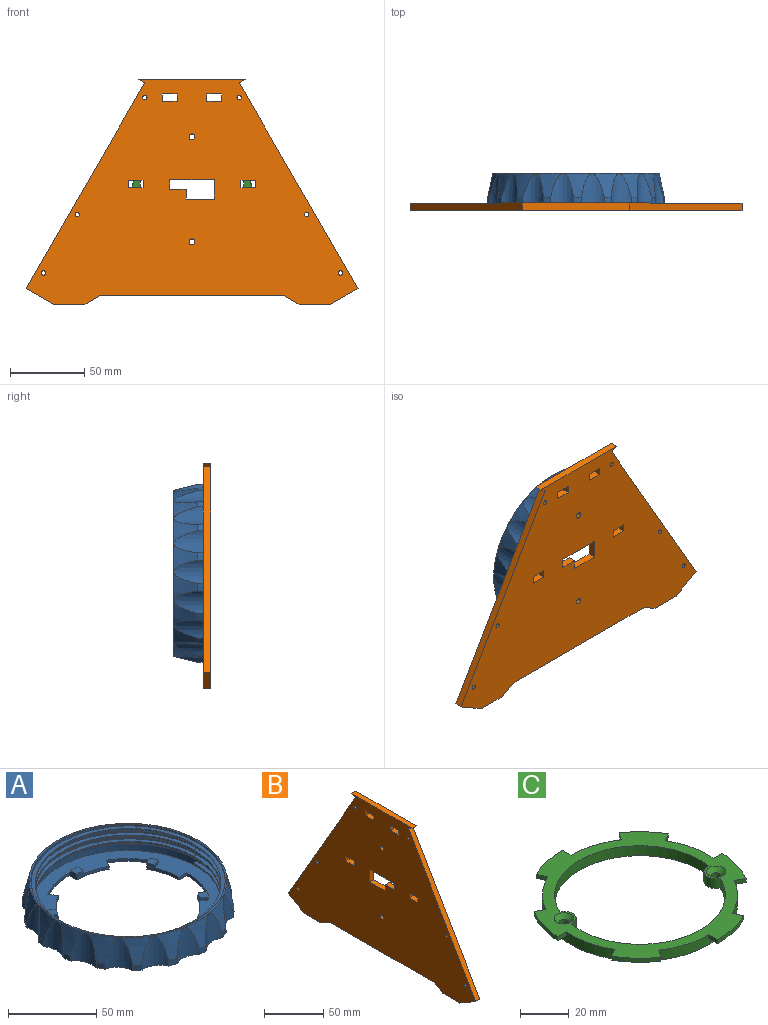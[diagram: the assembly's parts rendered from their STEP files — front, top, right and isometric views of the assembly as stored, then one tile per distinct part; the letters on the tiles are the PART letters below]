
ASSEMBLY  parts=3 mates=1
PART A: 105 faces, bbox 122.7x126.8x23 mm
  f0: plane 5.6x5.31mm, normal (0,0,1), area 26.5mm2, adj f1,f2,f3,f4
  f1: plane 4.96x2mm, normal (0.99,-0.12,0), area 10mm2, adj f0,f2,f4,f5
  f2: cylinder r=46mm len=5.6mm, axis (0,0,-1), area 11.2mm2, adj f0,f1,f3,f5
  f3: plane 6.25x4mm, normal (-1,0,0), area 22.5mm2, adj f0,f2,f4,f5,f37,f38,f48
  f4: cylinder r=41mm len=4.99mm, axis (0,0,-1), area 10mm2, adj f0,f1,f3,f5
  f5: plane 110x110mm, normal (0,0,1), area 3265.8mm2, adj f1,f2,f3,f4,f8,f10,f11,f12
  f6: cylinder r=55mm len=110mm, axis (0,0,-1), area 345.6mm2, adj f7,f9,f96,f98
  f7: cylinder r=55mm len=110mm, axis (0,0,-1), area 345.6mm2, adj f6,f8,f92,f94
  f8: cylinder r=55mm len=110mm, axis (0,0,-1), area 950.3mm2, adj f5,f7,f49,f50
  f9: cylinder r=55mm len=110mm, axis (0,0,-1), area 614.4mm2, adj f6,f99,f100,f102,f103
  f10: plane 5.41x4mm, normal (0.5,0.87,0), area 22.5mm2, adj f5,f11,f13,f14,f47,f48,f51
  f11: cylinder r=46mm len=4.68mm, axis (0,0,-1), area 11.2mm2, adj f5,f10,f12,f51
  f12: plane 3.99x3.01mm, normal (-0.6,-0.8,0), area 10mm2, adj f5,f11,f13,f51
  f13: cylinder r=41mm len=4.17mm, axis (0,0,-1), area 10mm2, adj f5,f10,f12,f51
  f14: cylinder r=40.75mm len=14.92mm, axis (0,0,-1), area 42.7mm2, adj f5,f10,f15,f48
  f15: plane 5.41x3.13mm, normal (-0.87,-0.5,0), area 12.5mm2, adj f5,f14,f16,f48
  f16: cylinder r=47mm len=23.5mm, axis (0,0,1), area 49.2mm2, adj f5,f15,f17,f48
  f17: plane 6.25x4mm, normal (1,0,0), area 22.5mm2, adj f5,f16,f18,f20,f21,f48,f52
  f18: cylinder r=46mm len=5.6mm, axis (0,0,-1), area 11.2mm2, adj f5,f17,f19,f52
  f19: plane 4.96x2mm, normal (-0.99,0.12,0), area 10mm2, adj f5,f18,f20,f52
  f20: cylinder r=41mm len=4.99mm, axis (0,0,-1), area 10mm2, adj f5,f17,f19,f52
  f21: cylinder r=40.75mm len=20.38mm, axis (0,0,-1), area 42.7mm2, adj f5,f17,f22,f48
  f22: plane 5.41x3.13mm, normal (-0.87,0.5,0), area 12.5mm2, adj f5,f21,f23,f48
  f23: cylinder r=47mm len=17.2mm, axis (0,0,1), area 49.2mm2, adj f5,f22,f24,f48
  f24: plane 5.41x4mm, normal (0.5,-0.87,0), area 22.5mm2, adj f5,f23,f25,f27,f28,f48,f53
  f25: cylinder r=46mm len=5.02mm, axis (0,0,-1), area 11.2mm2, adj f5,f24,f26,f53
  f26: plane 4.6x2mm, normal (-0.39,0.92,0), area 10mm2, adj f5,f25,f27,f53
  f27: cylinder r=41mm len=4.47mm, axis (0,0,-1), area 10mm2, adj f5,f24,f26,f53
  f28: cylinder r=40.75mm len=20.38mm, axis (0,0,-1), area 42.7mm2, adj f5,f24,f29,f48
  f29: plane 6.25x2mm, normal (0,1,0), area 12.5mm2, adj f5,f28,f30,f48
  f30: cylinder r=47mm len=23.5mm, axis (0,0,1), area 49.2mm2, adj f5,f29,f31,f48
  f31: plane 5.41x4mm, normal (-0.5,-0.87,0), area 22.5mm2, adj f5,f30,f32,f34,f35,f48,f54
  f32: cylinder r=46mm len=4.68mm, axis (0,0,-1), area 11.2mm2, adj f5,f31,f33,f54
  f33: plane 3.99x3.01mm, normal (0.6,0.8,0), area 10mm2, adj f5,f32,f34,f54
  f34: cylinder r=41mm len=4.17mm, axis (0,0,-1), area 10mm2, adj f5,f31,f33,f54
  f35: cylinder r=40.75mm len=14.92mm, axis (0,0,-1), area 42.7mm2, adj f5,f31,f36,f48
  f36: plane 5.41x3.13mm, normal (0.87,0.5,0), area 12.5mm2, adj f5,f35,f37,f48
  f37: cylinder r=47mm len=23.5mm, axis (0,0,1), area 49.2mm2, adj f3,f5,f36,f48
  f38: cylinder r=40.75mm len=20.38mm, axis (0,0,-1), area 42.7mm2, adj f3,f5,f39,f48
  f39: plane 5.41x3.13mm, normal (0.87,-0.5,0), area 12.5mm2, adj f5,f38,f40,f48
  f40: cylinder r=47mm len=17.2mm, axis (0,0,1), area 49.2mm2, adj f5,f39,f41,f48
  f41: plane 5.41x4mm, normal (-0.5,0.87,0), area 22.5mm2, adj f5,f40,f42,f44,f45,f48,f55
  f42: cylinder r=46mm len=5.02mm, axis (0,0,-1), area 11.2mm2, adj f5,f41,f43,f55
  f43: plane 4.6x2mm, normal (0.39,-0.92,0), area 10mm2, adj f5,f42,f44,f55
  f44: cylinder r=41mm len=4.47mm, axis (0,0,-1), area 10mm2, adj f5,f41,f43,f55
  f45: cylinder r=40.75mm len=20.38mm, axis (0,0,-1), area 42.7mm2, adj f5,f41,f46,f48
  f46: plane 6.25x2mm, normal (0,-1,0), area 12.5mm2, adj f5,f45,f47,f48
  f47: cylinder r=47mm len=23.5mm, axis (0,0,1), area 49.2mm2, adj f5,f10,f46,f48
  f48: plane 120x119mm, normal (0,0,-1), area 4655.6mm2, adj f3,f10,f14,f15,f16,f17,f21,f22
  f49: bspline ~126.76x117.75mm, area 1194.1mm2, adj f8,f50,f92,f93
  f50: plane 3.5x2.5mm, normal (0,1,0), area 5.6mm2, adj f8,f49,f93,f94
  f51: plane 7.18x7.09mm, normal (0,0,1), area 26.5mm2, adj f10,f11,f12,f13
  f52: plane 5.6x5.31mm, normal (0,0,1), area 26.5mm2, adj f17,f18,f19,f20
  f53: plane 6.97x6.83mm, normal (0,0,1), area 26.5mm2, adj f24,f25,f26,f27
  f54: plane 7.18x7.09mm, normal (0,0,1), area 26.5mm2, adj f31,f32,f33,f34
  f55: plane 6.97x6.83mm, normal (0,0,1), area 26.5mm2, adj f41,f42,f43,f44
  f56: cylinder r=60mm len=5.34mm, axis (0,0,1), area 19.1mm2, adj f48,f57,f91,f95
  f57: cone r=13mm half-angle=2.6deg, axis (0,0,1), area 245.3mm2, adj f48,f56,f58,f95
  f58: cylinder r=60mm len=4.69mm, axis (0,0,1), area 19.1mm2, adj f48,f57,f59,f95
  f59: cone r=13mm half-angle=2.6deg, axis (0,0,1), area 245.3mm2, adj f48,f58,f60,f95
  f60: cylinder r=60mm len=4.15mm, axis (0,0,1), area 19.1mm2, adj f48,f59,f61,f95
  f61: cone r=13mm half-angle=2.6deg, axis (0,0,1), area 245.3mm2, adj f48,f60,f62,f95
  f62: cylinder r=60mm len=5.09mm, axis (0,0,1), area 19.1mm2, adj f48,f61,f63,f95
  f63: cone r=13mm half-angle=2.6deg, axis (0,0,1), area 245.3mm2, adj f48,f62,f64,f95
  f64: cylinder r=60mm len=5.42mm, axis (0,0,1), area 19.1mm2, adj f48,f63,f65,f95
  f65: cone r=13mm half-angle=2.6deg, axis (0,0,1), area 245.3mm2, adj f48,f64,f66,f95
  f66: cylinder r=60mm len=5.09mm, axis (0,0,1), area 19.1mm2, adj f48,f65,f67,f95
  f67: cone r=13mm half-angle=2.6deg, axis (0,0,1), area 245.3mm2, adj f48,f66,f68,f95
  f68: cylinder r=60mm len=4.15mm, axis (0,0,1), area 19.1mm2, adj f48,f67,f69,f95
  f69: cone r=13mm half-angle=2.6deg, axis (0,0,1), area 245.3mm2, adj f48,f68,f70,f95
  f70: cylinder r=60mm len=4.69mm, axis (0,0,1), area 19.1mm2, adj f48,f69,f71,f95
  f71: cone r=13mm half-angle=2.6deg, axis (0,0,1), area 245.3mm2, adj f48,f70,f72,f95
  f72: cylinder r=60mm len=5.34mm, axis (0,0,1), area 19.1mm2, adj f48,f71,f73,f95
  f73: cone r=13mm half-angle=2.6deg, axis (0,0,1), area 245.3mm2, adj f48,f72,f74,f95
  f74: cylinder r=60mm len=5.34mm, axis (0,0,1), area 19.1mm2, adj f48,f73,f75,f95
  f75: cone r=13mm half-angle=2.6deg, axis (0,0,1), area 245.3mm2, adj f48,f74,f76,f95
  f76: cylinder r=60mm len=4.69mm, axis (0,0,1), area 19.1mm2, adj f48,f75,f77,f95
  f77: cone r=13mm half-angle=2.6deg, axis (0,0,1), area 245.3mm2, adj f48,f76,f78,f95
  f78: cylinder r=60mm len=4.15mm, axis (0,0,1), area 19.1mm2, adj f48,f77,f79,f95
  f79: cone r=13mm half-angle=2.6deg, axis (0,0,1), area 245.3mm2, adj f48,f78,f80,f95
  f80: cylinder r=60mm len=5.09mm, axis (0,0,1), area 19.1mm2, adj f48,f79,f81,f95
  f81: cone r=13mm half-angle=2.6deg, axis (0,0,1), area 245.3mm2, adj f48,f80,f82,f95
  f82: cylinder r=60mm len=5.42mm, axis (0,0,1), area 19.1mm2, adj f48,f81,f83,f95
  f83: cone r=13mm half-angle=2.6deg, axis (0,0,1), area 245.3mm2, adj f48,f82,f84,f95
  f84: cylinder r=60mm len=5.09mm, axis (0,0,1), area 19.1mm2, adj f48,f83,f85,f95
  f85: cone r=13mm half-angle=2.6deg, axis (0,0,1), area 245.3mm2, adj f48,f84,f86,f95
  f86: cylinder r=60mm len=4.15mm, axis (0,0,1), area 19.1mm2, adj f48,f85,f87,f95
  f87: cone r=13mm half-angle=2.6deg, axis (0,0,1), area 245.3mm2, adj f48,f86,f88,f95
  f88: cylinder r=60mm len=4.69mm, axis (0,0,1), area 19.1mm2, adj f48,f87,f89,f95
  f89: cone r=13mm half-angle=2.6deg, axis (0,0,1), area 245.3mm2, adj f48,f88,f90,f95
  f90: cylinder r=60mm len=5.34mm, axis (0,0,1), area 19.1mm2, adj f48,f89,f91,f95
  f91: cone r=13mm half-angle=2.6deg, axis (0,0,1), area 245.3mm2, adj f48,f56,f90,f95
  f92: bspline ~126.76x117.75mm, area 1194.1mm2, adj f7,f49,f96,f97
  f93: bspline ~120.78x112.2mm, area 329.9mm2, adj f49,f50,f94,f97
  f94: bspline ~126.76x117.75mm, area 844.4mm2, adj f7,f50,f93,f98
  f95: cone r=60mm half-angle=13.8deg, axis (0,0,-1), area 2860.6mm2, adj f56,f57,f58,f59,f60,f61,f62,f63
  f96: bspline ~126.76x117.75mm, area 1194.1mm2, adj f6,f92,f100,f101
  f97: bspline ~120.78x112.2mm, area 329.9mm2, adj f92,f93,f98,f101
  f98: bspline ~126.76x117.75mm, area 844.4mm2, adj f6,f94,f97,f102
  f99: plane 112x112mm, normal (0,0,1), area 348.7mm2, adj f9,f95
  f100: bspline ~126.76x117.75mm, area 466.9mm2, adj f9,f96,f103,f104
  f101: bspline ~120.78x112.2mm, area 320.7mm2, adj f96,f97,f102,f103,f104
  f102: bspline ~126.76x117.75mm, area 750.6mm2, adj f9,f98,f101,f103
  f103: plane 110x102.64mm, normal (0,0,1), area 424mm2, adj f9,f100,f101,f102,f104
  f104: bspline ~112.2x97.04mm, area 9.2mm2, adj f100,f101,f103
PART B: 44 faces, bbox 5x223.7x152.1 mm
  f0: plane 5x5mm, normal (0,-1,0), area 25mm2, adj f1,f33,f34,f35
  f1: plane 10x5mm, normal (0,0,1), area 50mm2, adj f0,f2,f34,f35
  f2: plane 5x5mm, normal (0,1,0), area 25mm2, adj f1,f33,f34,f35
  f3: plane 124.79x5mm, normal (0,0,-1), area 623.9mm2, adj f4,f22,f34,f35
  f4: plane 10.39x6mm, normal (0,-0.5,-0.87), area 60mm2, adj f3,f5,f34,f35
  f5: plane 20x5mm, normal (0,0,-1), area 100mm2, adj f4,f6,f34,f35
  f6: plane 19.05x11mm, normal (0,0.5,-0.87), area 110mm2, adj f5,f7,f34,f35
  f7: plane 138.56x80.03mm, normal (0,0.87,0.5), area 800mm2, adj f6,f8,f34,f35
  f8: plane 5x4.33mm, normal (0,0.5,-0.87), area 25mm2, adj f7,f9,f34,f35
  f9: plane 72.27x5mm, normal (0,0,1), area 361.3mm2, adj f8,f10,f34,f35
  f10: plane 5x4.33mm, normal (0,-0.5,-0.87), area 25mm2, adj f9,f11,f34,f35
  f11: plane 138.56x80.03mm, normal (0,-0.87,0.5), area 800mm2, adj f10,f12,f34,f35
  f12: plane 19.05x11mm, normal (0,-0.5,-0.87), area 110mm2, adj f11,f13,f34,f35
  f13: plane 20x5mm, normal (0,0,-1), area 100mm2, adj f12,f22,f34,f35
  f14: plane 10x5mm, normal (0,0,1), area 50mm2, adj f15,f23,f34,f35
  f15: plane 5x5mm, normal (0,1,0), area 25mm2, adj f14,f16,f34,f35
  f16: plane 10x5mm, normal (0,0,-1), area 50mm2, adj f15,f23,f34,f35
  f17: plane 11x5mm, normal (0,0,1), area 55mm2, adj f18,f32,f34,f35
  f18: plane 6.5x5mm, normal (0,1,0), area 32.5mm2, adj f17,f19,f34,f35
  f19: plane 30x5mm, normal (0,0,-1), area 150mm2, adj f18,f20,f34,f35
  f20: plane 13x5mm, normal (0,-1,0), area 65mm2, adj f19,f21,f34,f35
  f21: plane 19x5mm, normal (0,0,1), area 95mm2, adj f20,f32,f34,f35
  f22: plane 10.39x6mm, normal (0,0.5,-0.87), area 60mm2, adj f3,f13,f34,f35
  f23: plane 5x5mm, normal (0,-1,0), area 25mm2, adj f14,f16,f34,f35
  f24: cylinder r=1.5mm len=5mm, axis (-1,0,0), area 47.1mm2, adj f34,f35
  f25: cylinder r=1.5mm len=5mm, axis (-1,0,0), area 47.1mm2, adj f34,f35
  f26: cylinder r=1.5mm len=5mm, axis (-1,0,0), area 47.1mm2, adj f34,f35
  f27: cylinder r=1.5mm len=5mm, axis (-1,0,0), area 47.1mm2, adj f34,f35
  f28: cylinder r=1.5mm len=5mm, axis (-1,0,0), area 47.1mm2, adj f34,f35
  f29: cylinder r=1.5mm len=5mm, axis (-1,0,0), area 47.1mm2, adj f34,f35
  f30: cylinder r=2mm len=5mm, axis (-1,0,0), area 62.8mm2, adj f34,f35
  f31: cylinder r=2mm len=5mm, axis (-1,0,0), area 62.8mm2, adj f34,f35
  f32: plane 6.5x5mm, normal (0,1,0), area 32.5mm2, adj f17,f21,f34,f35
  f33: plane 10x5mm, normal (0,0,-1), area 50mm2, adj f0,f2,f34,f35
  f34: plane 223.66x152.06mm, normal (1,0,0), area 20925.7mm2, adj f0,f1,f2,f3,f4,f5,f6,f7
  f35: plane 223.66x152.06mm, normal (-1,0,0), area 20925.7mm2, adj f0,f1,f2,f3,f4,f5,f6,f7
  f36: plane 5x5mm, normal (0,1,0), area 25mm2, adj f34,f35,f37,f39
  f37: plane 10x5mm, normal (0,0,1), area 50mm2, adj f34,f35,f36,f38
  f38: plane 5x5mm, normal (0,-1,0), area 25mm2, adj f34,f35,f37,f39
  f39: plane 10x5mm, normal (0,0,-1), area 50mm2, adj f34,f35,f36,f38
  f40: plane 5x5mm, normal (0,1,0), area 25mm2, adj f34,f35,f41,f43
  f41: plane 10x5mm, normal (0,0,1), area 50mm2, adj f34,f35,f40,f42
  f42: plane 5x5mm, normal (0,-1,0), area 25mm2, adj f34,f35,f41,f43
  f43: plane 10x5mm, normal (0,0,-1), area 50mm2, adj f34,f35,f40,f42
PART C: 35 faces, bbox 89.8x90x5 mm
  f0: cylinder r=2mm len=4mm, axis (0,0,-1), area 37.7mm2, adj f1,f2
  f1: cone r=2mm half-angle=45deg, axis (0,0,1), area 53.3mm2, adj f0,f3
  f2: plane 80x80mm, normal (0,0,-1), area 1222.1mm2, adj f0,f4,f5,f6,f7,f8,f9
  f3: plane 90x89.78mm, normal (0,0,1), area 1725.2mm2, adj f1,f4,f5,f6,f7,f8,f10,f11
  f4: cylinder r=40mm len=80mm, axis (0,0,1), area 1038.8mm2, adj f2,f3,f10,f12,f13,f15,f16,f18
  f5: cylinder r=5mm len=9.53mm, axis (0,0,-1), area 71.4mm2, adj f2,f3,f6,f8
  f6: cylinder r=35mm len=66.69mm, axis (0,0,-1), area 500.1mm2, adj f2,f3,f5,f7
  f7: cylinder r=5mm len=9.53mm, axis (0,0,-1), area 71.4mm2, adj f2,f3,f6,f8
  f8: cylinder r=35mm len=66.69mm, axis (0,0,-1), area 500.1mm2, adj f2,f3,f5,f7
  f9: cylinder r=2mm len=4mm, axis (0,0,-1), area 37.7mm2, adj f2,f28
  f10: plane 4.15x2.8mm, normal (0.83,-0.56,0), area 10mm2, adj f3,f4,f11,f31
  f11: cylinder r=45mm len=14.81mm, axis (0,0,1), area 40.8mm2, adj f3,f10,f12,f31
  f12: plane 4.33x2.5mm, normal (-0.5,0.87,0), area 10mm2, adj f3,f4,f11,f31
  f13: plane 5x2mm, normal (-1,0,0), area 10mm2, adj f3,f4,f14,f30
  f14: cylinder r=45mm len=19.73mm, axis (0,0,1), area 40.8mm2, adj f3,f13,f16,f30
  f15: plane 4.99x2mm, normal (-0.07,-1,0), area 10mm2, adj f3,f4,f17,f32
  f16: plane 4.49x2.19mm, normal (0.9,0.44,0), area 10mm2, adj f3,f4,f14,f30
  f17: cylinder r=45mm len=19.36mm, axis (0,0,1), area 40.8mm2, adj f3,f15,f18,f32
  f18: plane 4.33x2.5mm, normal (0.5,0.87,0), area 10mm2, adj f3,f4,f17,f32
  f19: plane 4.33x2.5mm, normal (-0.5,-0.87,0), area 10mm2, adj f3,f4,f20,f29
  f20: cylinder r=45mm len=19.36mm, axis (0,0,1), area 40.8mm2, adj f3,f19,f22,f29
  f21: plane 4.49x2.19mm, normal (-0.9,-0.44,0), area 10mm2, adj f3,f4,f23,f33
  f22: plane 4.99x2mm, normal (0.07,1,0), area 10mm2, adj f3,f4,f20,f29
  f23: cylinder r=45mm len=19.73mm, axis (0,0,1), area 40.8mm2, adj f3,f21,f24,f33
  f24: plane 5x2mm, normal (1,0,0), area 10mm2, adj f3,f4,f23,f33
  f25: plane 4.33x2.5mm, normal (0.5,-0.87,0), area 10mm2, adj f3,f4,f26,f34
  f26: cylinder r=45mm len=14.81mm, axis (0,0,1), area 40.8mm2, adj f3,f25,f27,f34
  f27: plane 4.15x2.8mm, normal (-0.83,0.56,0), area 10mm2, adj f3,f4,f26,f34
  f28: cone r=2mm half-angle=45deg, axis (0,0,1), area 53.3mm2, adj f3,f9
  f29: plane 19.71x10.25mm, normal (0,0,-1), area 96.4mm2, adj f4,f19,f20,f22
  f30: plane 19.73x9.05mm, normal (0,0,-1), area 96.4mm2, adj f4,f13,f14,f16
  f31: plane 17.31x16.6mm, normal (0,0,-1), area 96.4mm2, adj f4,f10,f11,f12
  f32: plane 19.71x10.25mm, normal (0,0,-1), area 96.4mm2, adj f4,f15,f17,f18
  f33: plane 19.73x9.05mm, normal (0,0,-1), area 96.4mm2, adj f4,f21,f23,f24
  f34: plane 17.31x16.6mm, normal (0,0,-1), area 96.4mm2, adj f4,f25,f26,f27
PLACE A rot(axis=(-0.97,0.18,0.18),91.9deg) t=(-1.07,168.22,11.78)mm
PLACE B rot(axis=(0,0,-1),90deg) t=(-1.07,168.22,11.78)mm
PLACE C rot(axis=(-0.69,-0.51,-0.51),110.7deg) t=(-1.07,169.22,11.78)mm
MATE fastened C.f5 <-> B.f30  axis (0,-1,0) through (-1.07,168.22,47.14)mm
